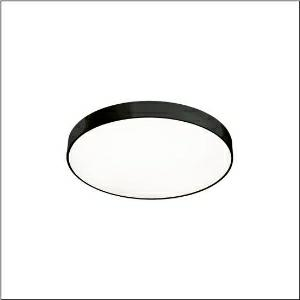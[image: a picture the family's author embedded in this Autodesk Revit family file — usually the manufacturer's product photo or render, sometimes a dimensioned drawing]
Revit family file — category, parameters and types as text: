
# Revit family: round_21_m_51mr36gd0321b
name_source: partatom
category: Lighting Fixtures
units: mm (PartAtom-declared; Revit-internal decimal feet)

## family parameters
Cut with Voids When Loaded = No
Host = Face
Light Source = No
Part Type = Normal
Room Calculation Point = No
Round Connector Dimension = Use Diameter
Shared = No

## types (1)
- Round 21 M (1 x LED, 7550 lm, 54.6 W, 3000K)
    Apparent Load = 55 VA
    CIE Flux Codes = 49 80 96 85 100
    Color Rendering = 80
    Color Temperature = 3000K
    Default Elevation = 1800 mm
    Description = Round 21 M, wall and ceiling luminaire, primary optical cover: cover, of PMMA, opal, light emission: direct/indirect distribution, primary light characteristic: symmetric, installation type: suspended mounting, surface-mounted, LED, rated luminous flux: 7.550lm, luminous efficacy: 138lm/W, light colour: 830, colour temperature: 3000K, control gear: DALI 2, with terminal, 5-pole, mains connection: 230V, AC, 50/60Hz, rated input power: 54.6W, housing, of aluminium, coated, black, diameter: 600mm, height: 62mm, protection rating (complete): IP40, insulation class (complete): insulation class I (protective earthing), certification: CE, impact resistance: IK04, permissible operating ambient temperature: -10..+35°C, packaging unit: 1 piece
    Height = 87 mm
    Lamp = 1 x LED
    Lamp Light Flux = 7550 lm
    Lamp Power = 54.6 W
    Lamp count = 1
    Length = 600 mm
    Luminous efficacy = 138 lm/W
    Manufacturer = Siteco
    ModVariant = No
    Model = 51MR36GD0321B
    Mounting Place = Ceiling
    Mounting Type = Surface mounted
    Number of Poles = 1
    OnlyDefault = Yes
    Power Factor = 1
    Product Name = Round 21 M
    Product group = wall and ceiling luminaire | ceiling mounted
    ProductGroupID = 304
    Protection Class = Protection class I
    Protection Degree = IP 40
    RLX_Detail_Level = 1
    RLX_Emergency_Light_Flux = 0 lm
    RLX_Emergency_Type = 0
    RLX_Emergency_Type_DB = No
    RlxData = <blob elided: 18153 chars, md5=fb59b616>
    Socket = socket
    Standby Power = 0 W
    System Light Flux = 7550 lm
    System Power = 55 W
    Type Comments = Product without accessories
    Type Image = l_1258332.jpg
    URL = http://relux.com
    VarID = ---
    Voltage = 0 V
    Weight = 0.00 kg
    Width = 0 mm  [stored 0 ft]

note: [stored X ft] marks values corroborated as IEEE doubles in the binary element streams (Revit-internal decimal feet)

## geometry (parser evidence)
native form markers: Blend x4, Sweep x13
no freeform markers — native parametric forms only
